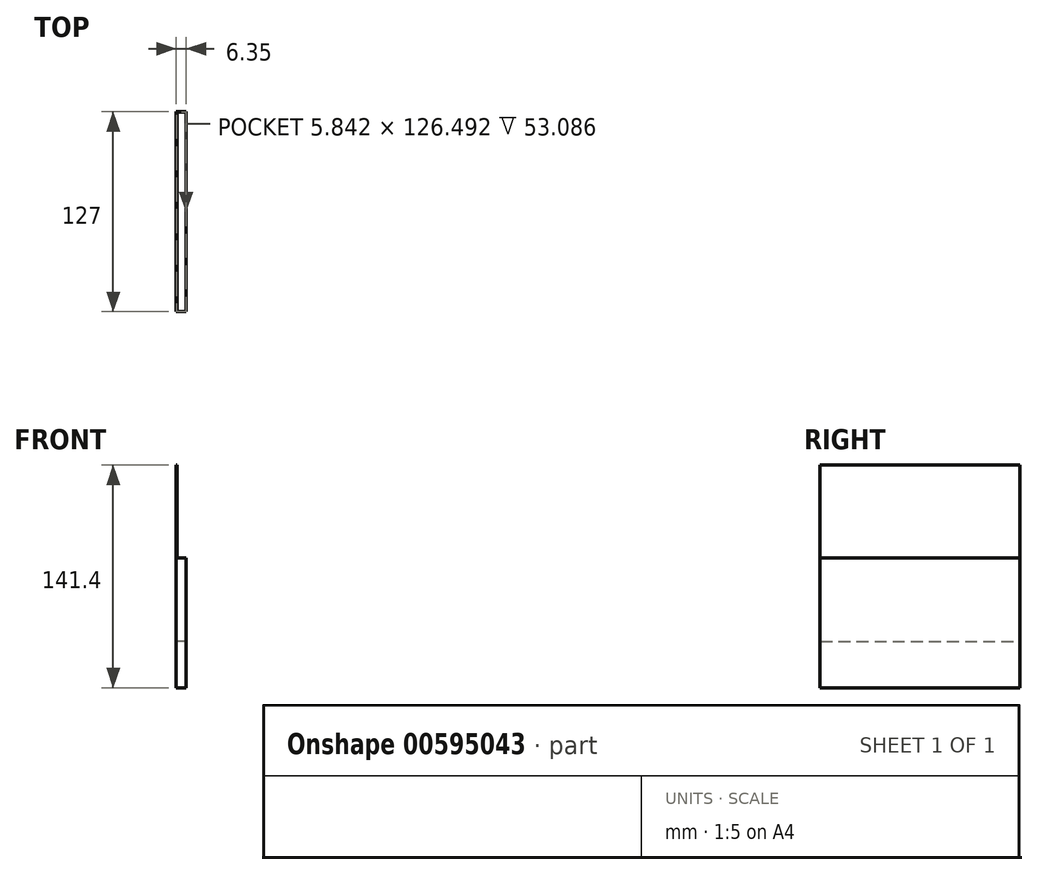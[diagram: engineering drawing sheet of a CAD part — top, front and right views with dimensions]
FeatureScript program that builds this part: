
annotation { "Feature Type Name" : "Feature", "Feature Type Description" : "" }
export const myFeature = defineFeature(function(context is Context, id is Id, definition is map)
    precondition{}
    {
        {
            var Q0;
            Q0=qCreatedBy(makeId("Front.planeOp"),FACE);
            var sketch = newSketch(context, id + "F0", { "sketchPlane" : qUnion([Q0])});
            skLineSegment(sketch, "E0", {"start": v(0, 0) * mm, "end": v(0, 57.15) * mm});
            skLineSegment(sketch, "E1", {"start": v(6.35, 57.15) * mm, "end": v(0, 57.15) * mm});
            skLineSegment(sketch, "E2", {"start": v(6.35, 57.15) * mm, "end": v(6.35, 0) * mm});
            skLineSegment(sketch, "E3", {"start": v(6.35, 0) * mm, "end": v(0, 0) * mm});
            skSolve(sketch);
        }
        {
            var Q0;
            Q0=makeQuery(id+"F0.imprint","IMPRINT",FACE,{"disambiguationData":[TD([[makeQuery(id+"F0.imprint","IMPRINT",EDGE,{"derivedFrom":sQuery(id+"F0.wireOp",EDGE,"E0")}),-1.0]])]});
            extrude(context, id + "F1", {"entities" : qUnion([Q0]), "depth" : 127 * mm, "offsetDistance" : 25.4 * mm});
        }
        {
            var Q0;
            Q0=makeQuery(id+"F1.opExtrude","SWEPT_FACE",FACE,{"disambiguationData":[OSD([sQuery(id+"F0.wireOp",EDGE,"E1")])]});
            var sketch = newSketch(context, id + "F2", { "sketchPlane" : qUnion([Q0])});
            skLineSegment(sketch, "E4.bottom", {"start": v(0, 0) * mm, "end": v(6.35, 0) * mm});
            skLineSegment(sketch, "E4.top", {"start": v(0, -127) * mm, "end": v(6.35, -127) * mm});
            skLineSegment(sketch, "E4.left", {"start": v(0, 0) * mm, "end": v(0, -127) * mm});
            skLineSegment(sketch, "E4.right", {"start": v(6.35, 0) * mm, "end": v(6.35, -127) * mm});
            skLineSegment(sketch, "E5.0", {"start": v(6.1, -0.25) * mm, "end": v(0.25, -0.25) * mm});
            skLineSegment(sketch, "E5.1", {"start": v(6.1, -126.75) * mm, "end": v(6.1, -0.25) * mm});
            skLineSegment(sketch, "E5.2", {"start": v(0.25, -126.75) * mm, "end": v(6.1, -126.75) * mm});
            skLineSegment(sketch, "E5.3", {"start": v(0.25, -0.25) * mm, "end": v(0.25, -126.75) * mm});
            skSolve(sketch);
        }
        {
            var Q0;
            Q0=makeQuery(id+"F2.imprint","IMPRINT",FACE,{"disambiguationData":[TD([[makeQuery(id+"F2.imprint","IMPRINT",EDGE,{"derivedFrom":sQuery(id+"F2.wireOp",EDGE,"E5.0")}),1.0]])]});
            extrude(context, id + "F3", {"entities" : qUnion([Q0]), "oppositeDirection" : true, "depth" : 53.1 * mm, "offsetDistance" : 25.4 * mm});
        }
        {
            var Q0;
            Q0=makeQuery(id+"F3.opExtrude","SWEPT_BODY",BODY,{"disambiguationData":[OSD([sQuery(id+"F2.wireOp",EDGE,"E5.0"),sQuery(id+"F2.wireOp",EDGE,"E5.1"),sQuery(id+"F2.wireOp",EDGE,"E5.2"),sQuery(id+"F2.wireOp",EDGE,"E5.3")])]});
            var Q1;
            Q1=makeQuery(id+"F1.opExtrude","SWEPT_BODY",BODY,{"disambiguationData":[OSD([sQuery(id+"F0.wireOp",EDGE,"E0"),sQuery(id+"F0.wireOp",EDGE,"E1"),sQuery(id+"F0.wireOp",EDGE,"E2"),sQuery(id+"F0.wireOp",EDGE,"E3")])]});
            booleanBodies(context, id + "F4", {"operationType" : BooleanOperationType.SUBTRACTION, "tools" : qUnion([Q0]), "targets" : qUnion([Q1])});
        }
        {
            var Q0;
            Q0=makeQuery(id+"F1.opExtrude","SWEPT_FACE",FACE,{"disambiguationData":[OSD([sQuery(id+"F0.wireOp",EDGE,"E3")])]});
            extrude(context, id + "F5", {"entities" : qUnion([Q0]), "operationType" : NewBodyOperationType.ADD, "depth" : 25.4 * mm, "offsetDistance" : 25.4 * mm});
        }
        {
            var Q0;
            Q0=makeQuery(id+"F5.opExtrude","CAP_FACE",FACE,{"disambiguationData":[OSD([sQuery(id+"F0.wireOp",EDGE,"E3")])],"isStart":false});
            var sketch = newSketch(context, id + "F6", { "sketchPlane" : qUnion([Q0])});
            skLineSegment(sketch, "E6.bottom", {"start": v(0, 51.66) * mm, "end": v(6.35, 51.66) * mm});
            skLineSegment(sketch, "E6.top", {"start": v(0, 76.24) * mm, "end": v(6.35, 76.24) * mm});
            skLineSegment(sketch, "E6.left", {"start": v(0, 51.66) * mm, "end": v(0, 76.24) * mm});
            skLineSegment(sketch, "E6.right", {"start": v(6.35, 51.66) * mm, "end": v(6.35, 76.24) * mm});
            skSolve(sketch);
        }
        {
            var Q0;
            Q0 = qSketchRegion(id + "F6", true);
            extrude(context, id + "F7", {"entities" : qUnion([Q0]), "operationType" : NewBodyOperationType.ADD, "oppositeDirection" : true, "depth" : 2.54 * mm, "offsetDistance" : 25.4 * mm});
        }
        {
            var Q0;
            {var subQ0=sQuery(id+"F0.wireOp",EDGE,"E0");Q0=makeQuery(id+"F5.boolean.opBoolean","MERGE",FACE,{"derivedFrom":[makeQuery(id+"F1.opExtrude","SWEPT_FACE",FACE,{"disambiguationData":[OSD([subQ0])]}),makeQuery(id+"F5.opExtrude","SWEPT_FACE",FACE,{"disambiguationData":[OSD([subQ0,sQuery(id+"F0.wireOp",EDGE,"E3")])]})]});}
            var sketch = newSketch(context, id + "F8", { "sketchPlane" : qUnion([Q0])});
            skLineSegment(sketch, "E7.bottom", {"start": v(127, 57.15) * mm, "end": v(0, 57.15) * mm});
            skLineSegment(sketch, "E7.top", {"start": v(127, 116) * mm, "end": v(0, 116) * mm});
            skLineSegment(sketch, "E7.left", {"start": v(127, 57.15) * mm, "end": v(127, 116) * mm});
            skLineSegment(sketch, "E7.right", {"start": v(0, 57.15) * mm, "end": v(0, 116) * mm});
            skSolve(sketch);
        }
        {
            var Q0;
            Q0 = qSketchRegion(id + "F8", true);
            extrude(context, id + "F9", {"entities" : qUnion([Q0]), "oppositeDirection" : true, "depth" : 0.5 * mm, "offsetDistance" : 25.4 * mm});
        }
    });
